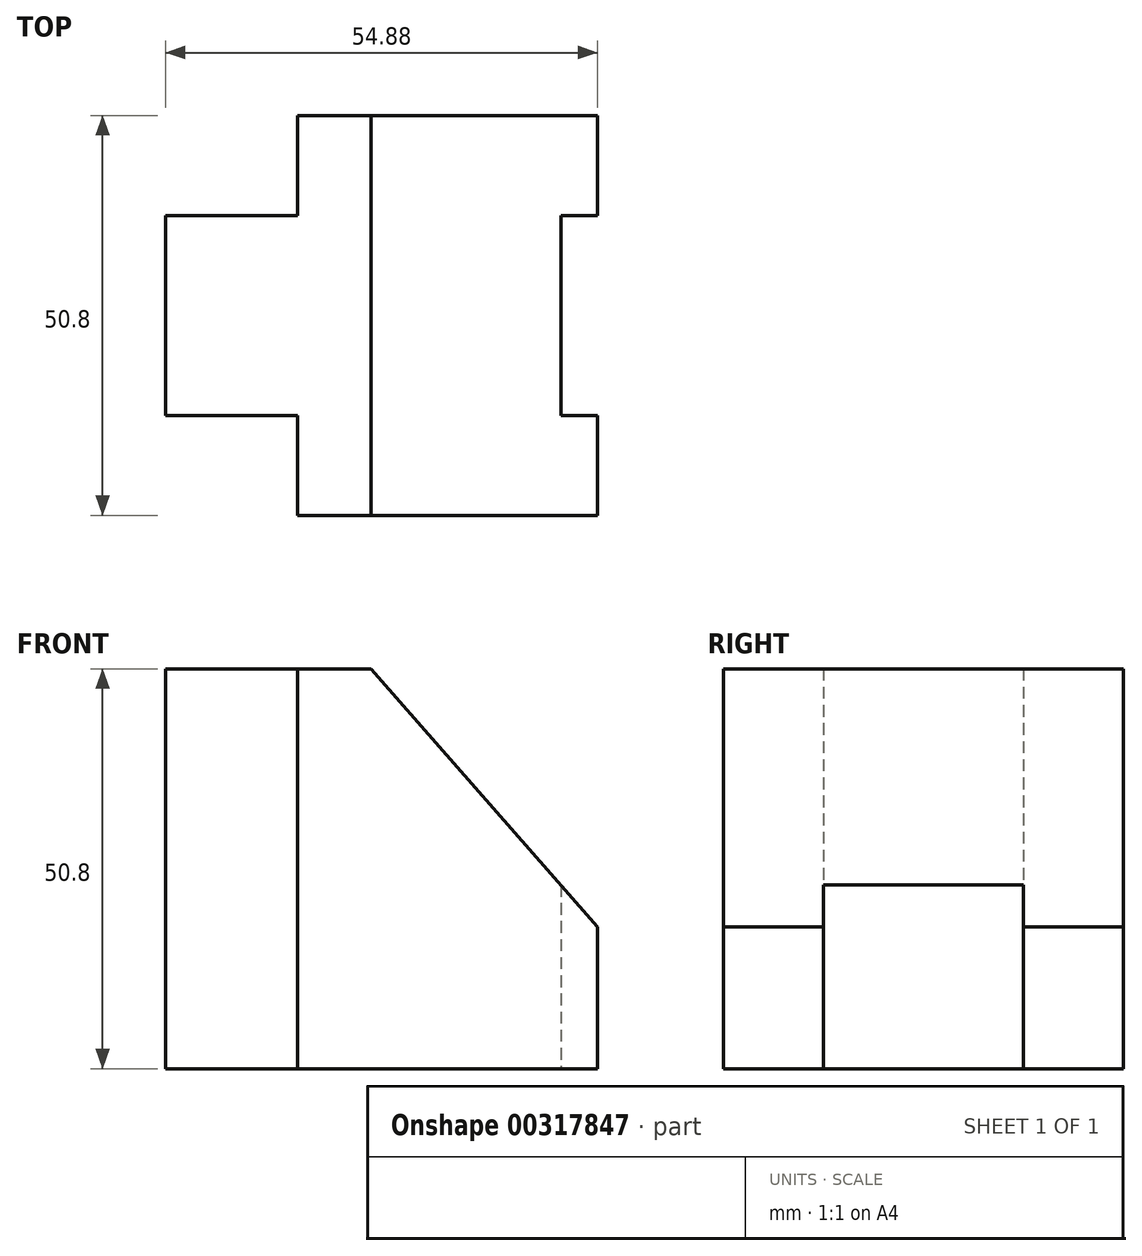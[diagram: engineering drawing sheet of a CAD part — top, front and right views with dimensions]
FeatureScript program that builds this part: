
annotation { "Feature Type Name" : "Feature", "Feature Type Description" : "" }
export const myFeature = defineFeature(function(context is Context, id is Id, definition is map)
    precondition{}
    {
        {
            var Q0;
            Q0=qCreatedBy(makeId("Top.planeOp"),FACE);
            var sketch = newSketch(context, id + "F0", { "sketchPlane" : qUnion([Q0])});
            skLineSegment(sketch, "E0", {"start": v(0, 38.1) * mm, "end": v(0, 12.7) * mm});
            skLineSegment(sketch, "E1", {"start": v(0, 12.7) * mm, "end": v(16.78, 12.7) * mm});
            skLineSegment(sketch, "E2", {"start": v(16.78, 12.7) * mm, "end": v(16.78, 0) * mm});
            skLineSegment(sketch, "E3", {"start": v(16.78, 0) * mm, "end": v(54.88, 0) * mm});
            skLineSegment(sketch, "E4", {"start": v(54.88, 0) * mm, "end": v(54.88, 12.7) * mm});
            skLineSegment(sketch, "E5", {"start": v(54.88, 12.7) * mm, "end": v(50.2, 12.7) * mm});
            skLineSegment(sketch, "E6", {"start": v(50.2, 12.7) * mm, "end": v(50.2, 38.1) * mm});
            skLineSegment(sketch, "E7", {"start": v(50.2, 38.1) * mm, "end": v(54.88, 38.1) * mm});
            skLineSegment(sketch, "E8", {"start": v(54.88, 38.1) * mm, "end": v(54.88, 50.8) * mm});
            skLineSegment(sketch, "E9", {"start": v(54.88, 50.8) * mm, "end": v(16.78, 50.8) * mm});
            skLineSegment(sketch, "E10", {"start": v(16.78, 50.8) * mm, "end": v(16.78, 38.1) * mm});
            skLineSegment(sketch, "E11", {"start": v(16.78, 38.1) * mm, "end": v(0, 38.1) * mm});
            skLineSegment(sketch, "E12", {"start": v(29.48, 50.8) * mm, "end": v(29.48, 0) * mm});
            skSolve(sketch);
        }
        {
            var Q0;
            Q0 = qSketchRegion(id + "F0", true);
            extrude(context, id + "F1", {"entities" : qUnion([Q0]), "depth" : 25.4 * mm});
        }
        {
            var Q0;
            Q0=makeQuery(id+"F1.opExtrude","CAP_FACE",FACE,{"disambiguationData":[OSD([sQuery(id+"F0.wireOp",EDGE,"E0"),sQuery(id+"F0.wireOp",EDGE,"E1"),sQuery(id+"F0.wireOp",EDGE,"E2"),sQuery(id+"F0.wireOp",EDGE,"E3"),sQuery(id+"F0.wireOp",EDGE,"E4"),sQuery(id+"F0.wireOp",EDGE,"E5"),sQuery(id+"F0.wireOp",EDGE,"E6"),sQuery(id+"F0.wireOp",EDGE,"E7"),sQuery(id+"F0.wireOp",EDGE,"E8"),sQuery(id+"F0.wireOp",EDGE,"E9"),sQuery(id+"F0.wireOp",EDGE,"E10"),sQuery(id+"F0.wireOp",EDGE,"E11")])],"isStart":false});
            extrude(context, id + "F2", {"entities" : qUnion([Q0]), "operationType" : NewBodyOperationType.ADD, "depth" : 25.4 * mm});
        }
        {
            var Q0;
            {var subQ0=sQuery(id+"F0.wireOp",EDGE,"E3");Q0=makeQuery(id+"F2.boolean.opBoolean","MERGE",FACE,{"derivedFrom":[makeQuery(id+"F1.opExtrude","SWEPT_FACE",FACE,{"disambiguationData":[OSD([subQ0])]}),makeQuery(id+"F2.opExtrude","SWEPT_FACE",FACE,{"disambiguationData":[OSD([subQ0])]})]});}
            var sketch = newSketch(context, id + "F3", { "sketchPlane" : qUnion([Q0])});
            skLineSegment(sketch, "E13", {"start": v(26.13, 50.8) * mm, "end": v(54.88, 18) * mm});
            skSolve(sketch);
        }
        {
            var Q0;
            {var subQ0=sQuery(id+"F3.wireOp",EDGE,"E13");Q0=makeQuery(id+"F3.imprint","IMPRINT",FACE,{"disambiguationData":[TD([[makeQuery(id+"F3.imprint","IMPRINT",EDGE,{"derivedFrom":subQ0}),1.0]])]});}
            extrude(context, id + "F4", {"entities" : qUnion([Q0]), "operationType" : NewBodyOperationType.REMOVE, "oppositeDirection" : true, "depth" : 68.58 * mm});
        }
    });
